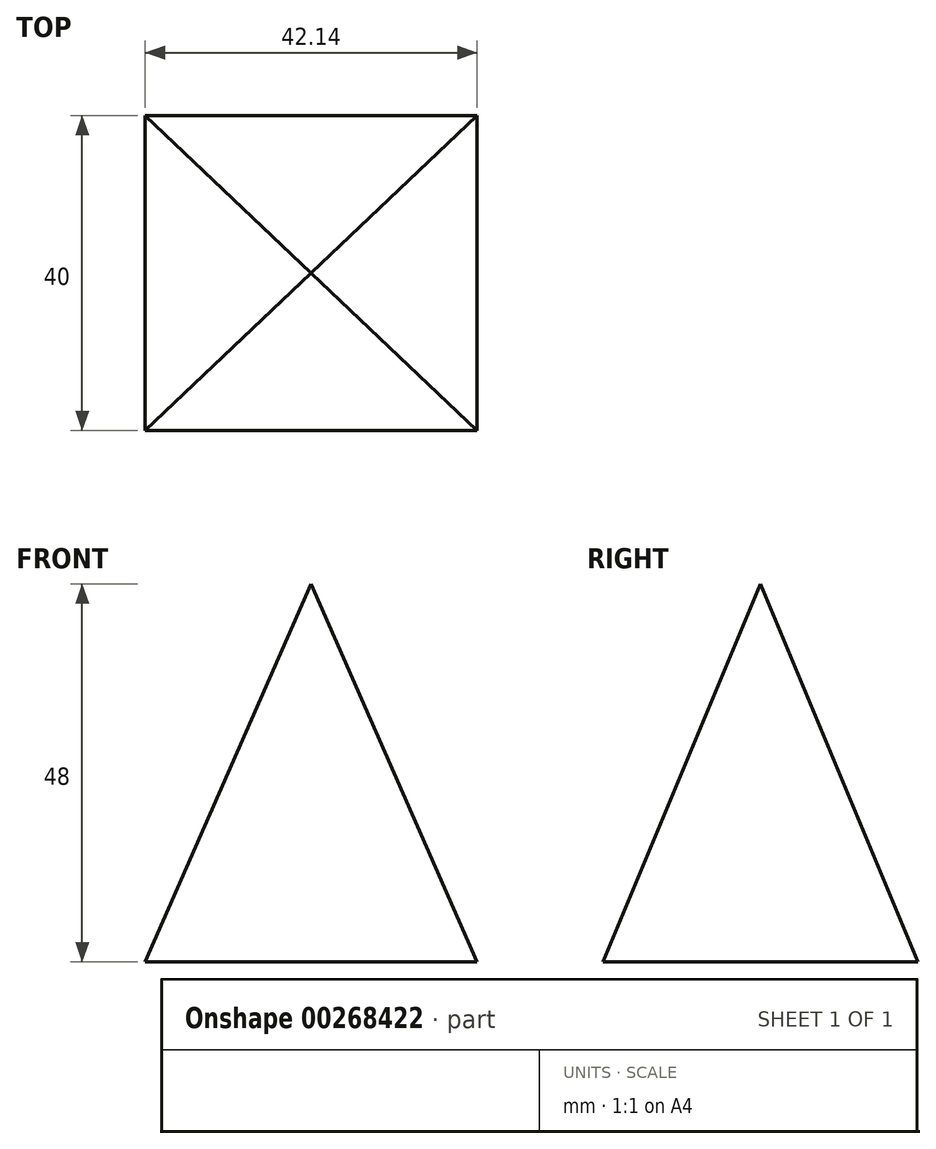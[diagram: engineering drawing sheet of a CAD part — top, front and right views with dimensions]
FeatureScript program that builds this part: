
annotation { "Feature Type Name" : "Feature", "Feature Type Description" : "" }
export const myFeature = defineFeature(function(context is Context, id is Id, definition is map)
    precondition{}
    {
        {
            var Q0;
            Q0=qCreatedBy(makeId("Top.planeOp"),FACE);
            var sketch = newSketch(context, id + "F0", { "sketchPlane" : qUnion([Q0])});
            skLineSegment(sketch, "E0.bottom", {"start": v(21.07, 20) * mm, "end": v(-21.07, 20) * mm});
            skLineSegment(sketch, "E0.top", {"start": v(21.07, -20) * mm, "end": v(-21.07, -20) * mm});
            skLineSegment(sketch, "E0.left", {"start": v(21.07, 20) * mm, "end": v(21.07, -20) * mm});
            skLineSegment(sketch, "E0.right", {"start": v(-21.07, 20) * mm, "end": v(-21.07, -20) * mm});
            skPoint(sketch, "E0.middle", {"position": v(0, 0) * mm});
            skLineSegment(sketch, "E1", {"start": v(21.07, -20) * mm, "end": v(21.07, 20) * mm});
            skSolve(sketch);
        }
        {
            var Q0;
            Q0=qCreatedBy(makeId("Top.planeOp"),FACE);
            cPlane(context, id + "F1", {"entities" : qUnion([Q0]), "cplaneType" : CPlaneType.OFFSET, "offset" : 48 * mm, "width" : 152.4 * mm, "height" : 152.4 * mm});
        }
        {
            var Q0;
            Q0=qCreatedBy(id+"F1.planeOp",FACE);
            var sketch = newSketch(context, id + "F2", { "sketchPlane" : qUnion([Q0])});
            skPoint(sketch, "E2", {"position": v(0, 0) * mm});
            skSolve(sketch);
        }
        {
            var Q0;
            Q0=makeQuery(id+"F0.imprint","IMPRINT",FACE,{"disambiguationData":[TD([[makeQuery(id+"F0.imprint","IMPRINT",EDGE,{"derivedFrom":sQuery(id+"F0.wireOp",EDGE,"E0.bottom")}),1.0]])]});
            var Q1;
            Q1=sQuery(id+"F2.wireOp",VERTEX,"E2");
            loft(context, id + "F3", {"sheetProfilesArray" : [{ "sheetProfileEntities" : qUnion([Q0]) }, { "sheetProfileEntities" : qUnion([Q1]) }]});
        }
    });
